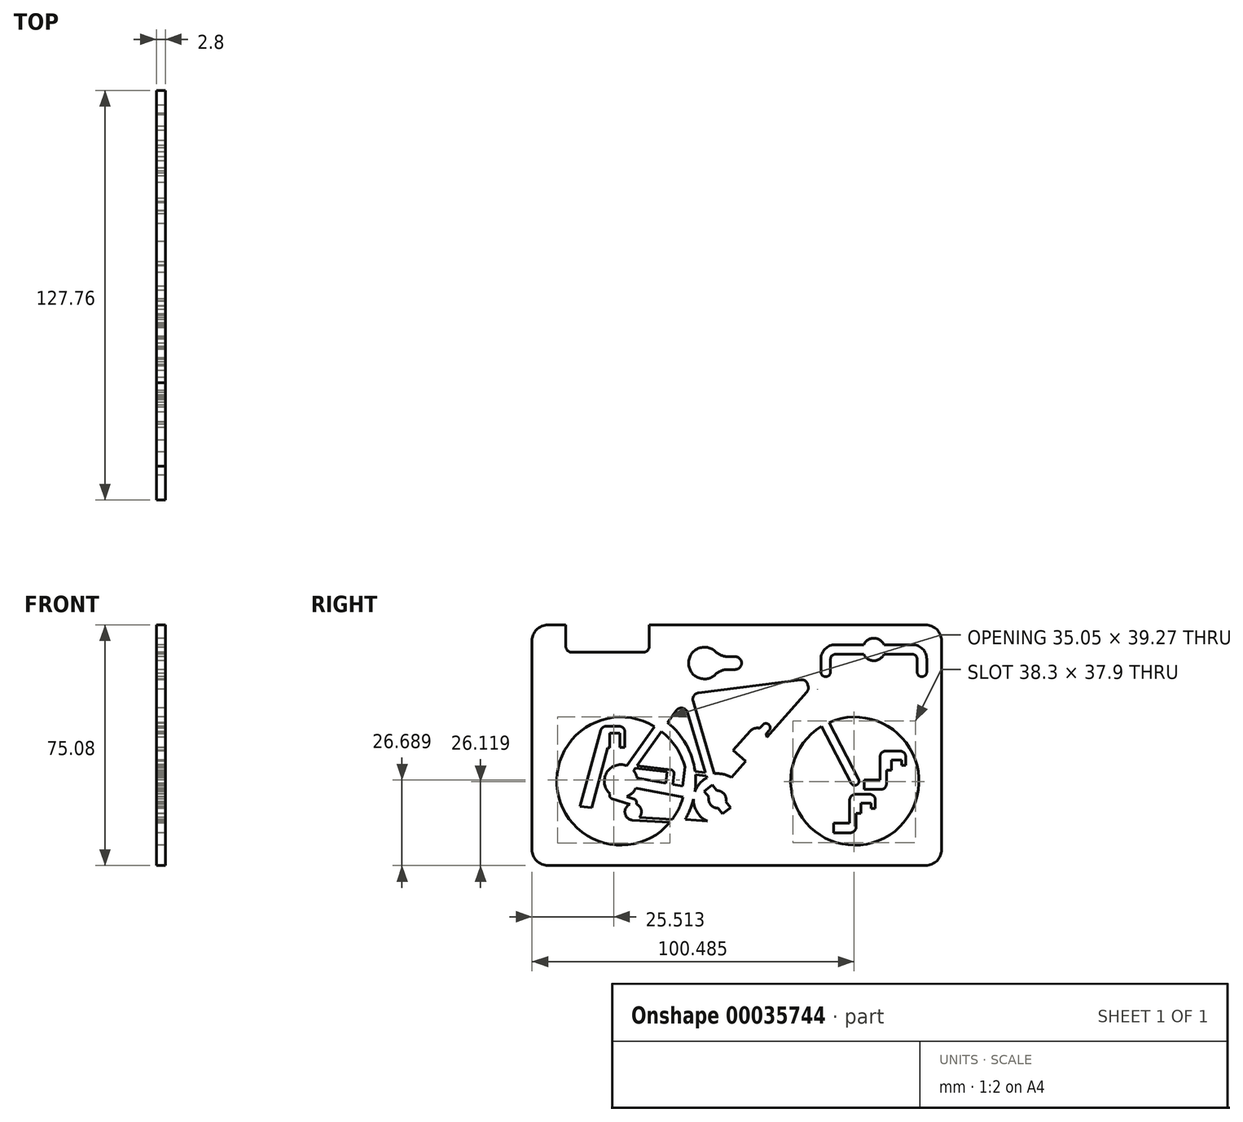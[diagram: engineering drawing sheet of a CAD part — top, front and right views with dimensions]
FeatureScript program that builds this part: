
annotation { "Feature Type Name" : "Feature", "Feature Type Description" : "" }
export const myFeature = defineFeature(function(context is Context, id is Id, definition is map)
    precondition{}
    {
        {
            assignVariable(context, id + "F0", {"name" : "H", "anyValue" : 2.8});
        }
        {
            var Q0;
            Q0=qCreatedBy(makeId("Right.planeOp"),FACE);
            var sketch = newSketch(context, id + "F1", { "sketchPlane" : qUnion([Q0])});
            skArc(sketch, "E0", {"start": v(-24.13, -6.05) * mm, "mid": v(-23.9, -3.4) * mm, "end": v(-23.98, -0.75) * mm});
            skLineSegment(sketch, "E1.0.left", {"start": v(-28.58, 25.85) * mm, "end": v(-32.78, 40.06) * mm});
            skLineSegment(sketch, "E1.0.right", {"start": v(-26.16, 27.08) * mm, "end": v(-30, 40.23) * mm});
            skLineSegment(sketch, "E2.0.startCap", {"start": v(-28.4, 25.23) * mm, "end": v(-28.4, 25.23) * mm});
            skLineSegment(sketch, "E2.0.left", {"start": v(-24.73, 22.24) * mm, "end": v(-18.03, -0.43) * mm});
            skLineSegment(sketch, "E2.0.right", {"start": v(-26.45, 18.66) * mm, "end": v(-20.9, -0.08) * mm});
            skLineSegment(sketch, "E2.1.endCap", {"start": v(-25.84, 25.99) * mm, "end": v(-25.84, 25.99) * mm});
            skLineSegment(sketch, "E2.1.left", {"start": v(-45.44, 2.11) * mm, "end": v(-36.77, 14.32) * mm});
            skLineSegment(sketch, "E2.2.startCap", {"start": v(-28.4, 25.23) * mm, "end": v(-28.4, 25.23) * mm});
            skLineSegment(sketch, "E2.2.endCap", {"start": v(12.78, 30.97) * mm, "end": v(12.78, 30.97) * mm});
            skLineSegment(sketch, "E2.2.left", {"start": v(-26.16, 27.08) * mm, "end": v(9.78, 31.72) * mm});
            skArc(sketch, "E2.3.endCap", {"start": v(14.25, 26) * mm, "mid": v(14.25, 25.99) * mm, "end": v(14.25, 25.98) * mm});
            skLineSegment(sketch, "E2.3.right", {"start": v(-10.81, -3.35) * mm, "end": v(12.38, 22.92) * mm});
            skLineSegment(sketch, "E2.4.left", {"start": v(10.82, 37.6) * mm, "end": v(12.78, 30.97) * mm});
            skLineSegment(sketch, "E2.4.right", {"start": v(8.04, 37.6) * mm, "end": v(9.78, 31.72) * mm});
            skLineSegment(sketch, "E2.5.startCap", {"start": v(10.22, 30.22) * mm, "end": v(10.22, 30.22) * mm});
            skLineSegment(sketch, "E2.5.left", {"start": v(12.78, 30.97) * mm, "end": v(16.41, 18.68) * mm});
            skLineSegment(sketch, "E2.5.right", {"start": v(11.03, 27.5) * mm, "end": v(11.17, 27) * mm});
            skArc(sketch, "E2.6.endCap", {"start": v(26.9, -2.1) * mm, "mid": v(26.33, -3.9) * mm, "end": v(24.53, -3.33) * mm});
            skLineSegment(sketch, "E2.6.left", {"start": v(17.7, 15.6) * mm, "end": v(26.9, -2.1) * mm});
            skLineSegment(sketch, "E2.6.right", {"start": v(15.34, 14.38) * mm, "end": v(24.53, -3.33) * mm});
            skArc(sketch, "E3", {"start": v(15.34, 14.38) * mm, "mid": v(34.93, -20.47) * mm, "end": v(17.7, 15.6) * mm});
            skArc(sketch, "E4", {"start": v(-45.44, 2.11) * mm, "mid": v(-51.68, -0.11) * mm, "end": v(-50.57, -6.64) * mm});
            skLineSegment(sketch, "E5.0.right", {"start": v(-42.59, -4.95) * mm, "end": v(-27.87, -7.72) * mm});
            skLineSegment(sketch, "E6.trimOffspring", {"start": v(-23.07, 24.79) * mm, "end": v(8.85, 28.9) * mm});
            skLineSegment(sketch, "E7.trimOffspring", {"start": v(-43.27, 0.57) * mm, "end": v(-42.74, 1.31) * mm});
            skArc(sketch, "E8.trimOffspring", {"start": v(-42.19, -1.68) * mm, "mid": v(-42.59, -0.49) * mm, "end": v(-43.27, 0.57) * mm});
            skArc(sketch, "E9.trimOffspring", {"start": v(-36.77, 14.32) * mm, "mid": v(-66.97, -5.92) * mm, "end": v(-31.92, -15.58) * mm});
            skArc(sketch, "E10.trimOffspring", {"start": v(-34.83, 17.05) * mm, "mid": v(-70.04, -7.66) * mm, "end": v(-27.76, -15.58) * mm});
            skLineSegment(sketch, "E11.trimOffspring", {"start": v(-32.66, 15.5) * mm, "end": v(-30, 19.25) * mm});
            skLineSegment(sketch, "E12.trimOffspring", {"start": v(-34.83, 17.05) * mm, "end": v(-28.58, 25.85) * mm});
            skLineSegment(sketch, "E13.trimOffspring", {"start": v(-12.8, -1.58) * mm, "end": v(-9.7, 1.94) * mm});
            skLineSegment(sketch, "E14.trimOffspring", {"start": v(12.38, 22.92) * mm, "end": v(14, 17.45) * mm});
            skArc(sketch, "E15.trimOffspring", {"start": v(14, 17.45) * mm, "mid": v(36.24, -23.54) * mm, "end": v(16.41, 18.68) * mm});
            skArc(sketch, "E16", {"start": v(-24.58, -8.33) * mm, "mid": v(-23.45, -12.4) * mm, "end": v(-20.3, -15.22) * mm});
            skLineSegment(sketch, "E17", {"start": v(-43.4, -10.23) * mm, "end": v(-43.4, -10.23) * mm});
            skArc(sketch, "E18.0.endCap", {"start": v(-50.06, -8.17) * mm, "mid": v(-50.7, -7.54) * mm, "end": v(-50.57, -6.64) * mm});
            skArc(sketch, "E18.1.startCap", {"start": v(-50.06, -8.17) * mm, "mid": v(-50.7, -7.54) * mm, "end": v(-50.57, -6.64) * mm});
            skArc(sketch, "E18.1.endCap", {"start": v(-43.1, -8.28) * mm, "mid": v(-42.59, -8.64) * mm, "end": v(-42.4, -9.23) * mm});
            skLineSegment(sketch, "E18.1.right", {"start": v(-50.06, -8.17) * mm, "end": v(-44.44, -9.95) * mm});
            skLineSegment(sketch, "E18.2.left", {"start": v(-42.4, -9.23) * mm, "end": v(-42.4, -9.93) * mm});
            skArc(sketch, "E19.trimOffspring", {"start": v(-45.42, -7.54) * mm, "mid": v(-43.75, -6.52) * mm, "end": v(-42.59, -4.95) * mm});
            skLineSegment(sketch, "E20.trimOffspring", {"start": v(-45.42, -7.54) * mm, "end": v(-43.1, -8.28) * mm});
            skPoint(sketch, "E21.visualSharp", {"position": v(-25.4, 24.49) * mm});
            skArc(sketch, "E21.filletArc", {"start": v(-23.07, 24.79) * mm, "mid": v(-24.49, 23.9) * mm, "end": v(-24.73, 22.24) * mm});
            skPoint(sketch, "E22.visualSharp", {"position": v(-27.62, 22.6) * mm});
            skArc(sketch, "E22.filletArc", {"start": v(-26.45, 18.66) * mm, "mid": v(-28.04, 20.06) * mm, "end": v(-30, 19.25) * mm});
            skPoint(sketch, "E23.visualSharp", {"position": v(10.54, 29.13) * mm});
            skArc(sketch, "E23.filletArc", {"start": v(11.03, 27.5) * mm, "mid": v(10.2, 28.6) * mm, "end": v(8.85, 28.9) * mm});
            skPoint(sketch, "E24.visualSharp", {"position": v(11.49, 25.94) * mm});
            skArc(sketch, "E24.filletArc", {"start": v(10.75, 25.11) * mm, "mid": v(11.2, 26) * mm, "end": v(11.17, 27) * mm});
            skArc(sketch, "E25.trimOffspring", {"start": v(-20.43, -1.7) * mm, "mid": v(-22.71, -3.5) * mm, "end": v(-24.13, -6.05) * mm});
            skArc(sketch, "E26.0.endCap", {"start": v(-6.97, 12.85) * mm, "mid": v(-5.59, 13.74) * mm, "end": v(-3.94, 13.76) * mm});
            skLineSegment(sketch, "E26.0.left", {"start": v(-12.2, 6.92) * mm, "end": v(-6.97, 12.85) * mm});
            skLineSegment(sketch, "E27.trimOffspring", {"start": v(-1.72, 10.98) * mm, "end": v(10.75, 25.11) * mm});
            skLineSegment(sketch, "E28", {"start": v(-12.2, 6.92) * mm, "end": v(-8.33, 3.5) * mm});
            skLineSegment(sketch, "E29", {"start": v(-9.7, 1.94) * mm, "end": v(-8.33, 3.5) * mm});
            skArc(sketch, "E30.0.endCap", {"start": v(-3, 14.84) * mm, "mid": v(-1.11, 14.95) * mm, "end": v(-1, 13.07) * mm});
            skLineSegment(sketch, "E30.0.left", {"start": v(-3.94, 13.76) * mm, "end": v(-3, 14.84) * mm});
            skLineSegment(sketch, "E30.0.right", {"start": v(-1.94, 12) * mm, "end": v(-1, 13.07) * mm});
            skArc(sketch, "E31.trimOffspring", {"start": v(-1.94, 12) * mm, "mid": v(-1.79, 11.5) * mm, "end": v(-1.72, 10.98) * mm});
            skArc(sketch, "E32.0.endCap", {"start": v(-11.57, 36.12) * mm, "mid": v(-9.57, 34.12) * mm, "end": v(-11.57, 32.12) * mm});
            skLineSegment(sketch, "E32.0.left", {"start": v(-13.75, 36.12) * mm, "end": v(-11.57, 36.12) * mm});
            skLineSegment(sketch, "E32.0.right", {"start": v(-13.75, 32.12) * mm, "end": v(-11.57, 32.12) * mm});
            skPoint(sketch, "E33.visualSharp", {"position": v(-17.03, 36.12) * mm});
            skArc(sketch, "E33.filletArc", {"start": v(-17.4, 37.36) * mm, "mid": v(-15.68, 36.44) * mm, "end": v(-13.75, 36.12) * mm});
            skPoint(sketch, "E34.visualSharp", {"position": v(-17.03, 32.12) * mm});
            skArc(sketch, "E34.filletArc", {"start": v(-13.75, 32.12) * mm, "mid": v(-15.68, 31.8) * mm, "end": v(-17.4, 30.88) * mm});
            skLineSegment(sketch, "E35", {"start": v(-32.78, 40.06) * mm, "end": v(-32.78, 43.03) * mm});
            skLineSegment(sketch, "E36", {"start": v(-32.78, 43.03) * mm, "end": v(-30, 43.03) * mm});
            skLineSegment(sketch, "E37", {"start": v(-30, 43.03) * mm, "end": v(-30, 40.23) * mm});
            skLineSegment(sketch, "E38.rect.bottom", {"start": v(-22.8, 35.76) * mm, "end": v(-19.51, 35.76) * mm});
            skLineSegment(sketch, "E38.rect.top", {"start": v(-22.8, 32.47) * mm, "end": v(-19.51, 32.47) * mm});
            skLineSegment(sketch, "E38.rect.left", {"start": v(-22.8, 35.76) * mm, "end": v(-22.8, 32.47) * mm});
            skLineSegment(sketch, "E38.rect.right", {"start": v(-19.51, 35.76) * mm, "end": v(-19.51, 32.47) * mm});
            skPoint(sketch, "E38.rect.middle", {"position": v(-21.16, 34.12) * mm});
            skLineSegment(sketch, "E39", {"start": v(8.04, 37.6) * mm, "end": v(8.04, 40.4) * mm});
            skLineSegment(sketch, "E40", {"start": v(10.82, 37.6) * mm, "end": v(10.82, 40.4) * mm});
            skLineSegment(sketch, "E41", {"start": v(10.82, 40.4) * mm, "end": v(8.04, 40.4) * mm});
            skLineSegment(sketch, "E42.1.startCap", {"start": v(-20.7, -0.1) * mm, "end": v(-20.7, -0.1) * mm});
            skLineSegment(sketch, "E42.1.left", {"start": v(-20.6, -1.12) * mm, "end": v(-23.98, -0.75) * mm});
            skLineSegment(sketch, "E42.1.right", {"start": v(-20.9, -0.08) * mm, "end": v(-24.09, 0.27) * mm});
            skLineSegment(sketch, "E42.2.left", {"start": v(-41.45, -14.01) * mm, "end": v(-31.17, -14.62) * mm});
            skLineSegment(sketch, "E42.2.right", {"start": v(-43.68, -14.88) * mm, "end": v(-31.92, -15.58) * mm});
            skArc(sketch, "E42.3.right", {"start": v(-44.44, -9.95) * mm, "mid": v(-45.92, -12.84) * mm, "end": v(-43.4, -14.9) * mm});
            skArc(sketch, "E42.4.startCap", {"start": v(-17.41, -16.44) * mm, "mid": v(-17.42, -16.43) * mm, "end": v(-17.43, -16.43) * mm});
            skLineSegment(sketch, "E42.4.left", {"start": v(-17.43, -16.43) * mm, "end": v(-27.76, -15.58) * mm});
            skArc(sketch, "E42.5.right", {"start": v(-17.41, -16.44) * mm, "mid": v(-9.88, -12.02) * mm, "end": v(-10.81, -3.35) * mm});
            skArc(sketch, "E42.6.right", {"start": v(-12.8, -1.58) * mm, "mid": v(-15.32, -0.56) * mm, "end": v(-18.03, -0.43) * mm});
            skArc(sketch, "E43.trimOffspring", {"start": v(-24.09, 0.27) * mm, "mid": v(-26.9, 8.72) * mm, "end": v(-32.66, 15.5) * mm});
            skLineSegment(sketch, "E44.trimOffspring", {"start": v(-20.6, -1.12) * mm, "end": v(-20.43, -1.7) * mm});
            skLineSegment(sketch, "E45.trimOffspring", {"start": v(-42.17, 2.12) * mm, "end": v(-34.6, 12.78) * mm});
            skArc(sketch, "E46.trimOffspring", {"start": v(-41.45, -14.01) * mm, "mid": v(-40.88, -11.73) * mm, "end": v(-42.4, -9.93) * mm});
            skArc(sketch, "E47.trimOffspring", {"start": v(-31.17, -14.62) * mm, "mid": v(-29.19, -11.33) * mm, "end": v(-27.87, -7.72) * mm});
            skArc(sketch, "E48.trimOffspring", {"start": v(-27.16, -14.62) * mm, "mid": v(-25.64, -11.57) * mm, "end": v(-24.58, -8.33) * mm});
            skLineSegment(sketch, "E49.trimOffspring", {"start": v(-20.3, -15.22) * mm, "end": v(-27.16, -14.62) * mm});
            skPoint(sketch, "E42.2.endCap.center.orphan", {"position": v(-31.53, -15.1) * mm});
            skPoint(sketch, "E42.4.endCap.center.orphan", {"position": v(-27.45, -15.1) * mm});
            skArc(sketch, "E50.trimOffspring", {"start": v(-17.89, -15.9) * mm, "mid": v(-17.89, -15.9) * mm, "end": v(-17.89, -15.9) * mm});
            skLineSegment(sketch, "E51.rect.bottom", {"start": v(26.14, -12.83) * mm, "end": v(27.64, -12.83) * mm});
            skLineSegment(sketch, "E51.rect.top", {"start": v(26.14, -6.83) * mm, "end": v(30.34, -6.83) * mm});
            skLineSegment(sketch, "E51.rect.right", {"start": v(32.14, -11.23) * mm, "end": v(32.14, -8.62) * mm});
            skPoint(sketch, "E51.rect.middle", {"position": v(29.14, -9.83) * mm});
            skLineSegment(sketch, "E52.0.left", {"start": v(30.84, -9.63) * mm, "end": v(30.84, -11.23) * mm});
            skLineSegment(sketch, "E52.0.right", {"start": v(27.64, -9.63) * mm, "end": v(27.64, -12.83) * mm});
            skPoint(sketch, "E52.0.endCap.center.orphan", {"position": v(29.14, -12.83) * mm});
            skLineSegment(sketch, "E53.rect.top", {"start": v(-51.76, 14.4) * mm, "end": v(-47.77, 14.4) * mm});
            skLineSegment(sketch, "E54.0.left", {"start": v(-47.56, 12.2) * mm, "end": v(-47.56, 7.8) * mm});
            skLineSegment(sketch, "E53.rect.bottom", {"start": v(-51.4, 7.66) * mm, "end": v(-50.76, 7.66) * mm});
            skLineSegment(sketch, "E54.0.right", {"start": v(-50.76, 12.2) * mm, "end": v(-50.76, 7.66) * mm});
            skPoint(sketch, "E53.rect.middle", {"position": v(-48.46, 11.03) * mm});
            skLineSegment(sketch, "E55.bottom", {"start": v(26.14, -6.83) * mm, "end": v(25.93, -6.83) * mm});
            skLineSegment(sketch, "E55.left", {"start": v(26.14, -12.83) * mm, "end": v(26.14, -17.03) * mm});
            skLineSegment(sketch, "E55.right", {"start": v(24.14, -8.62) * mm, "end": v(24.14, -15.83) * mm});
            skLineSegment(sketch, "E56.top", {"start": v(24.14, -15.83) * mm, "end": v(19.14, -15.83) * mm});
            skLineSegment(sketch, "E56.right", {"start": v(19.14, -18.83) * mm, "end": v(19.14, -15.83) * mm});
            skLineSegment(sketch, "E57", {"start": v(19.14, -18.83) * mm, "end": v(24.34, -18.83) * mm});
            skPoint(sketch, "E58.visualSharp", {"position": v(26.14, -18.83) * mm});
            skArc(sketch, "E58.filletArc", {"start": v(24.34, -18.83) * mm, "mid": v(25.6, -18.3) * mm, "end": v(26.14, -17.03) * mm});
            skPoint(sketch, "E59.visualSharp", {"position": v(32.14, -6.83) * mm});
            skArc(sketch, "E59.filletArc", {"start": v(32.14, -8.62) * mm, "mid": v(31.6, -7.35) * mm, "end": v(30.34, -6.83) * mm});
            skPoint(sketch, "E60.visualSharp", {"position": v(24.14, -6.83) * mm});
            skArc(sketch, "E60.filletArc", {"start": v(25.93, -6.83) * mm, "mid": v(24.66, -7.35) * mm, "end": v(24.14, -8.62) * mm});
            skPoint(sketch, "E61.visualSharp", {"position": v(24.14, -15.83) * mm});
            skLineSegment(sketch, "E62", {"start": v(27.64, -9.63) * mm, "end": v(30.84, -9.63) * mm});
            skLineSegment(sketch, "E63", {"start": v(-51.4, 7.66) * mm, "end": v(-56.37, -10.97) * mm});
            skLineSegment(sketch, "E64", {"start": v(-60.02, -10.55) * mm, "end": v(-53.5, 13.08) * mm});
            skPoint(sketch, "E65.visualSharp", {"position": v(-53.13, 14.4) * mm});
            skArc(sketch, "E65.filletArc", {"start": v(-51.76, 14.4) * mm, "mid": v(-52.85, 14.03) * mm, "end": v(-53.5, 13.08) * mm});
            skPoint(sketch, "E66.visualSharp", {"position": v(-45.51, 14.4) * mm});
            skArc(sketch, "E66.filletArc", {"start": v(-45.97, 12.6) * mm, "mid": v(-46.5, 13.87) * mm, "end": v(-47.77, 14.4) * mm});
            skLineSegment(sketch, "E67", {"start": v(-50.76, 12.2) * mm, "end": v(-47.56, 12.2) * mm});
            skLineSegment(sketch, "E68", {"start": v(30.84, -11.23) * mm, "end": v(32.14, -11.23) * mm});
            skPoint(sketch, "E69.trimOffspring.end.orphan", {"position": v(32.14, -12.83) * mm});
            skPoint(sketch, "E70.trimOffspring.end.orphan", {"position": v(41.61, 0.67) * mm});
            skPoint(sketch, "E71.visualSharp", {"position": v(41.61, 6.67) * mm});
            skPoint(sketch, "E72.0.endCap.center.orphan", {"position": v(38.61, 0.67) * mm});
            skPoint(sketch, "E73.rect.middle", {"position": v(38.61, 3.67) * mm});
            skLineSegment(sketch, "E73.rect.top", {"start": v(35.61, 6.67) * mm, "end": v(39.81, 6.67) * mm});
            skPoint(sketch, "E74.visualSharp", {"position": v(35.61, -5.33) * mm});
            skLineSegment(sketch, "E75.left", {"start": v(35.61, 0.67) * mm, "end": v(35.61, -3.53) * mm});
            skPoint(sketch, "E76.visualSharp", {"position": v(33.61, -2.33) * mm});
            skPoint(sketch, "E77.visualSharp", {"position": v(33.61, 6.67) * mm});
            skLineSegment(sketch, "E75.right", {"start": v(33.61, 4.87) * mm, "end": v(33.61, -2.33) * mm});
            skLineSegment(sketch, "E78", {"start": v(28.61, -5.33) * mm, "end": v(33.81, -5.33) * mm});
            skLineSegment(sketch, "E79.top", {"start": v(33.61, -2.33) * mm, "end": v(28.61, -2.33) * mm});
            skLineSegment(sketch, "E73.rect.right", {"start": v(41.61, 2.27) * mm, "end": v(41.61, 4.87) * mm});
            skArc(sketch, "E71.filletArc", {"start": v(41.61, 4.87) * mm, "mid": v(41.09, 6.14) * mm, "end": v(39.81, 6.67) * mm});
            skLineSegment(sketch, "E80", {"start": v(40.31, 2.27) * mm, "end": v(41.61, 2.27) * mm});
            skLineSegment(sketch, "E81", {"start": v(37.11, 3.87) * mm, "end": v(40.31, 3.87) * mm});
            skLineSegment(sketch, "E72.0.right", {"start": v(37.11, 3.87) * mm, "end": v(37.11, 0.67) * mm});
            skLineSegment(sketch, "E73.rect.bottom", {"start": v(35.61, 0.67) * mm, "end": v(37.11, 0.67) * mm});
            skArc(sketch, "E74.filletArc", {"start": v(33.81, -5.33) * mm, "mid": v(35.09, -4.8) * mm, "end": v(35.61, -3.53) * mm});
            skArc(sketch, "E77.filletArc", {"start": v(35.41, 6.67) * mm, "mid": v(34.14, 6.14) * mm, "end": v(33.61, 4.87) * mm});
            skLineSegment(sketch, "E79.right", {"start": v(28.61, -5.33) * mm, "end": v(28.61, -2.33) * mm});
            skLineSegment(sketch, "E72.0.left", {"start": v(40.31, 3.87) * mm, "end": v(40.31, 2.27) * mm});
            skLineSegment(sketch, "E75.bottom", {"start": v(35.61, 6.67) * mm, "end": v(35.41, 6.67) * mm});
            skArc(sketch, "E82.0.endCap", {"start": v(18.16, 31.37) * mm, "mid": v(16.66, 29.87) * mm, "end": v(15.16, 31.37) * mm});
            skArc(sketch, "E82.5.endCap", {"start": v(48.16, 31.37) * mm, "mid": v(46.66, 29.87) * mm, "end": v(45.16, 31.37) * mm});
            skLineSegment(sketch, "E82.0.right", {"start": v(15.16, 35.37) * mm, "end": v(15.16, 31.37) * mm});
            skLineSegment(sketch, "E82.0.left", {"start": v(18.16, 35.37) * mm, "end": v(18.16, 31.37) * mm});
            skLineSegment(sketch, "E82.5.right", {"start": v(45.16, 35.37) * mm, "end": v(45.16, 31.37) * mm});
            skLineSegment(sketch, "E82.5.left", {"start": v(48.16, 35.37) * mm, "end": v(48.16, 31.37) * mm});
            skArc(sketch, "E83", {"start": v(28.5, 36.87) * mm, "mid": v(31.66, 34.87) * mm, "end": v(34.83, 36.87) * mm});
            skArc(sketch, "E82.1.right", {"start": v(19.66, 39.87) * mm, "mid": v(16.48, 38.55) * mm, "end": v(15.16, 35.37) * mm});
            skArc(sketch, "E82.1.left", {"start": v(19.66, 36.87) * mm, "mid": v(18.6, 36.43) * mm, "end": v(18.16, 35.37) * mm});
            skLineSegment(sketch, "E84.trimOffspring", {"start": v(28.5, 36.87) * mm, "end": v(19.66, 36.87) * mm});
            skLineSegment(sketch, "E85.trimOffspring", {"start": v(34.83, 36.87) * mm, "end": v(43.66, 36.87) * mm});
            skArc(sketch, "E82.4.left", {"start": v(45.16, 35.37) * mm, "mid": v(44.72, 36.43) * mm, "end": v(43.66, 36.87) * mm});
            skArc(sketch, "E82.4.right", {"start": v(48.16, 35.37) * mm, "mid": v(46.84, 38.55) * mm, "end": v(43.66, 39.87) * mm});
            skPoint(sketch, "E86.visualSharp", {"position": v(16.66, 38.37) * mm});
            skPoint(sketch, "E87.visualSharp", {"position": v(46.66, 38.37) * mm});
            skLineSegment(sketch, "E88.trimOffspring", {"start": v(28.5, 39.87) * mm, "end": v(19.66, 39.87) * mm});
            skLineSegment(sketch, "E89.trimOffspring", {"start": v(34.83, 39.87) * mm, "end": v(43.66, 39.87) * mm});
            skArc(sketch, "E90.trimOffspring", {"start": v(34.83, 39.87) * mm, "mid": v(31.66, 41.87) * mm, "end": v(28.5, 39.87) * mm});
            skLineSegment(sketch, "E91.bottom", {"start": v(-69.96, -29.05) * mm, "end": v(47.8, -29.05) * mm});
            skLineSegment(sketch, "E91.top", {"start": v(-69.96, 46.03) * mm, "end": v(47.8, 46.03) * mm});
            skLineSegment(sketch, "E91.left", {"start": v(-74.96, -24.05) * mm, "end": v(-74.96, 41.03) * mm});
            skLineSegment(sketch, "E91.right", {"start": v(52.8, -24.05) * mm, "end": v(52.8, 41.03) * mm});
            skPoint(sketch, "E92.visualSharp", {"position": v(-74.96, 46.03) * mm});
            skArc(sketch, "E92.filletArc", {"start": v(-69.96, 46.03) * mm, "mid": v(-73.5, 44.56) * mm, "end": v(-74.96, 41.03) * mm});
            skPoint(sketch, "E93.visualSharp", {"position": v(-74.96, -29.05) * mm});
            skArc(sketch, "E93.filletArc", {"start": v(-74.96, -24.05) * mm, "mid": v(-73.5, -27.58) * mm, "end": v(-69.96, -29.05) * mm});
            skPoint(sketch, "E94.visualSharp", {"position": v(52.8, 46.03) * mm});
            skArc(sketch, "E94.filletArc", {"start": v(52.8, 41.03) * mm, "mid": v(51.33, 44.56) * mm, "end": v(47.8, 46.03) * mm});
            skPoint(sketch, "E95.visualSharp", {"position": v(52.8, -29.05) * mm});
            skArc(sketch, "E95.filletArc", {"start": v(47.8, -29.05) * mm, "mid": v(51.33, -27.58) * mm, "end": v(52.8, -24.05) * mm});
            skArc(sketch, "E96", {"start": v(-17.4, 37.36) * mm, "mid": v(-26.11, 34.12) * mm, "end": v(-17.4, 30.88) * mm});
            skLineSegment(sketch, "E97", {"start": v(-47.56, 7.8) * mm, "end": v(-45.97, 7.8) * mm});
            skPoint(sketch, "E98.orphan", {"position": v(-47.56, 3.4) * mm});
            skLineSegment(sketch, "E99", {"start": v(-45.97, 12.6) * mm, "end": v(-45.97, 7.8) * mm});
            skLineSegment(sketch, "E100.bottom", {"start": v(-64.46, 46.03) * mm, "end": v(-38.35, 46.03) * mm});
            skLineSegment(sketch, "E100.top", {"start": v(-62.46, 37.48) * mm, "end": v(-40.35, 37.48) * mm});
            skLineSegment(sketch, "E100.left", {"start": v(-64.46, 46.03) * mm, "end": v(-64.46, 39.48) * mm});
            skLineSegment(sketch, "E100.right", {"start": v(-38.35, 46.03) * mm, "end": v(-38.35, 39.48) * mm});
            skText(sketch, "E101", { "text": "BULU", "fontName": "OpenSans-Bold.ttf"});
            skPoint(sketch, "E102.visualSharp", {"position": v(-38.35, 37.48) * mm});
            skArc(sketch, "E102.filletArc", {"start": v(-40.35, 37.48) * mm, "mid": v(-38.93, 38.06) * mm, "end": v(-38.35, 39.48) * mm});
            skPoint(sketch, "E103.visualSharp", {"position": v(-64.46, 37.48) * mm});
            skArc(sketch, "E103.filletArc", {"start": v(-64.46, 39.48) * mm, "mid": v(-63.87, 38.06) * mm, "end": v(-62.46, 37.48) * mm});
            skLineSegment(sketch, "E104.trimOffspring", {"start": v(-31.7, 0.85) * mm, "end": v(-42.17, 2.12) * mm});
            skLineSegment(sketch, "E105.0", {"start": v(-16.97, -11.15) * mm, "end": v(-15.5, -12.96) * mm});
            skArc(sketch, "E105.1", {"start": v(-19.77, -7.69) * mm, "mid": v(-19.22, -10.1) * mm, "end": v(-16.97, -11.15) * mm});
            skLineSegment(sketch, "E105.2", {"start": v(-19.77, -7.69) * mm, "end": v(-21.2, -5.92) * mm});
            skLineSegment(sketch, "E105.3", {"start": v(-21.2, -5.92) * mm, "end": v(-18.71, -3.9) * mm});
            skLineSegment(sketch, "E105.4", {"start": v(-17.28, -5.68) * mm, "end": v(-18.71, -3.9) * mm});
            skLineSegment(sketch, "E105.5", {"start": v(-15.5, -12.96) * mm, "end": v(-13.02, -10.95) * mm});
            skArc(sketch, "E105.6", {"start": v(-14.48, -9.14) * mm, "mid": v(-15.03, -6.72) * mm, "end": v(-17.28, -5.68) * mm});
            skLineSegment(sketch, "E105.7", {"start": v(-14.48, -9.14) * mm, "end": v(-13.02, -10.95) * mm});
            skLineSegment(sketch, "E106.0", {"start": v(30.02, 40) * mm, "end": v(33.22, 40) * mm});
            skLineSegment(sketch, "E106.1", {"start": v(30.02, 40) * mm, "end": v(30.02, 36.72) * mm});
            skLineSegment(sketch, "E106.2", {"start": v(30.02, 36.72) * mm, "end": v(33.22, 36.72) * mm});
            skLineSegment(sketch, "E106.3", {"start": v(33.22, 40) * mm, "end": v(33.22, 36.72) * mm});
            skLineSegment(sketch, "E107.0", {"start": v(-69.96, -31.05) * mm, "end": v(47.8, -31.05) * mm});
            skArc(sketch, "E107.1", {"start": v(-76.96, -24.05) * mm, "mid": v(-74.91, -29) * mm, "end": v(-69.96, -31.05) * mm});
            skLineSegment(sketch, "E107.2", {"start": v(-76.96, -24.05) * mm, "end": v(-76.96, 41.03) * mm});
            skArc(sketch, "E107.3", {"start": v(-69.96, 48.03) * mm, "mid": v(-74.91, 45.98) * mm, "end": v(-76.96, 41.03) * mm});
            skLineSegment(sketch, "E107.4", {"start": v(-69.96, 48.03) * mm, "end": v(47.8, 48.03) * mm});
            skArc(sketch, "E107.5", {"start": v(47.8, -31.05) * mm, "mid": v(52.75, -29) * mm, "end": v(54.8, -24.05) * mm});
            skArc(sketch, "E107.6", {"start": v(54.8, 41.03) * mm, "mid": v(52.75, 45.98) * mm, "end": v(47.8, 48.03) * mm});
            skLineSegment(sketch, "E107.7", {"start": v(54.8, -24.05) * mm, "end": v(54.8, 41.03) * mm});
            skPoint(sketch, "E108.end.orphan", {"position": v(-52.92, 14.4) * mm});
            skPoint(sketch, "E109.visualSharp", {"position": v(-30.15, 0.66) * mm});
            skArc(sketch, "E110.trimOffspring", {"start": v(-27.3, 1.71) * mm, "mid": v(-30, 7.87) * mm, "end": v(-34.6, 12.78) * mm});
            skLineSegment(sketch, "E111", {"start": v(-28.01, -4.26) * mm, "end": v(-31.04, -3.7) * mm});
            skLineSegment(sketch, "E112", {"start": v(-28.01, -4.26) * mm, "end": v(-27.3, 1.71) * mm});
            skLineSegment(sketch, "E113", {"start": v(-31.04, -3.7) * mm, "end": v(-30.65, -0.48) * mm});
            skLineSegment(sketch, "E114.trimOffspring", {"start": v(-32.75, 0.22) * mm, "end": v(-42.74, 1.31) * mm});
            skLineSegment(sketch, "E115", {"start": v(-33.18, -3.32) * mm, "end": v(-32.75, 0.22) * mm});
            skPoint(sketch, "E116.visualSharp", {"position": v(-30.51, 0.7) * mm});
            skArc(sketch, "E116.filletArc", {"start": v(-30.65, -0.48) * mm, "mid": v(-30.9, 0.4) * mm, "end": v(-31.7, 0.85) * mm});
            skLineSegment(sketch, "E117", {"start": v(-60.02, -10.55) * mm, "end": v(-56.37, -10.97) * mm});
            skLineSegment(sketch, "E118.trimOffspring", {"start": v(-33.18, -3.32) * mm, "end": v(-42.19, -1.68) * mm});
            const initialGuessF1  = {"E101": [-0.06296, 0.03873, 1, 0, 0.0062]};
            skSetInitialGuess(sketch, initialGuessF1);
            skSolve(sketch);
        }
        {
            var Q0;
            Q0=makeQuery(id+"F1.imprint","IMPRINT",FACE,{"disambiguationData":[TD([[makeQuery(id+"F1.imprint","IMPRINT",EDGE,{"derivedFrom":sQuery(id+"F1.wireOp",EDGE,"d670718d-e32d-4bfd-a30b-cf72b9636345")}),1.0]])]});
            var Q1;
            Q1=makeQuery(id+"F1.imprint","IMPRINT",FACE,{"disambiguationData":[TD([[makeQuery(id+"F1.imprint","IMPRINT",EDGE,{"derivedFrom":sQuery(id+"F1.wireOp",EDGE,"4c950c17-0d4c-4f3a-b05d-0eab68311945")}),1.0]])]});
            var Q2;
            Q2=makeQuery(id+"F1.imprint","IMPRINT",FACE,{"disambiguationData":[TD([[makeQuery(id+"F1.imprint","IMPRINT",EDGE,{"derivedFrom":sQuery(id+"F1.wireOp",EDGE,"E0")}),1.0]])]});
            var Q3;
            Q3=makeQuery(id+"F1.imprint","IMPRINT",FACE,{"disambiguationData":[TD([[makeQuery(id+"F1.imprint","IMPRINT",EDGE,{"derivedFrom":sQuery(id+"F1.wireOp",EDGE,"feb6c065-ad3e-4e5b-ba5c-cb6fa5ef12440.MirrorCS")}),-1.0]])]});
            var Q4;
            Q4=makeQuery(id+"F1.imprint","IMPRINT",FACE,{"disambiguationData":[TD([[makeQuery(id+"F1.imprint","IMPRINT",EDGE,{"derivedFrom":sQuery(id+"F1.wireOp",EDGE,"E53.rect.left")}),-1.0]])]});
            var Q5;
            Q5=makeQuery(id+"F1.imprint","IMPRINT",FACE,{"disambiguationData":[TD([[makeQuery(id+"F1.imprint","IMPRINT",EDGE,{"derivedFrom":sQuery(id+"F1.wireOp",EDGE,"E51.rect.bottom")}),1.0]])]});
            var Q6;
            Q6=makeQuery(id+"F1.imprint","IMPRINT",FACE,{"disambiguationData":[TD([[makeQuery(id+"F1.imprint","IMPRINT",EDGE,{"derivedFrom":sQuery(id+"F1.wireOp",EDGE,"6e1ddf8b-da26-4d41-9c80-b6f64bdec91b.rect.right")}),1.0]])]});
            var Q7;
            Q7=makeQuery(id+"F1.imprint","IMPRINT",FACE,{"disambiguationData":[TD([[makeQuery(id+"F1.imprint","IMPRINT",EDGE,{"derivedFrom":sQuery(id+"F1.wireOp",EDGE,"E54.0.startCap")}),1.0]])]});
            var Q8;
            Q8=makeQuery(id+"F1.imprint","IMPRINT",FACE,{"disambiguationData":[TD([[makeQuery(id+"F1.imprint","IMPRINT",EDGE,{"derivedFrom":sQuery(id+"F1.wireOp",EDGE,"E53.rect.top")}),-1.0]])]});
            var Q9;
            Q9=makeQuery(id+"F1.imprint","IMPRINT",FACE,{"disambiguationData":[TD([[makeQuery(id+"F1.imprint","IMPRINT",EDGE,{"derivedFrom":sQuery(id+"F1.wireOp",EDGE,"E32.0.endCap")}),-1.0]])]});
            var Q10;
            Q10=makeQuery(id+"F1.imprint","IMPRINT",FACE,{"disambiguationData":[TD([[makeQuery(id+"F1.imprint","IMPRINT",EDGE,{"derivedFrom":sQuery(id+"F1.wireOp",EDGE,"E82.0.endCap")}),-1.0]])]});
            var Q11;
            Q11=makeQuery(id+"F1.imprint","IMPRINT",FACE,{"disambiguationData":[TD([[makeQuery(id+"F1.imprint","IMPRINT",EDGE,{"derivedFrom":sQuery(id+"F1.wireOp",EDGE,"E73.rect.top")}),-1.0]])]});
            extrude(context, id + "F2", {"entities" : qUnion([Q0, Q1, Q2, Q3, Q4, Q5, Q6, Q7, Q8, Q9, Q10, Q11]), "depth" : (getVariable(context, 'H')) * mm});
        }
    });
